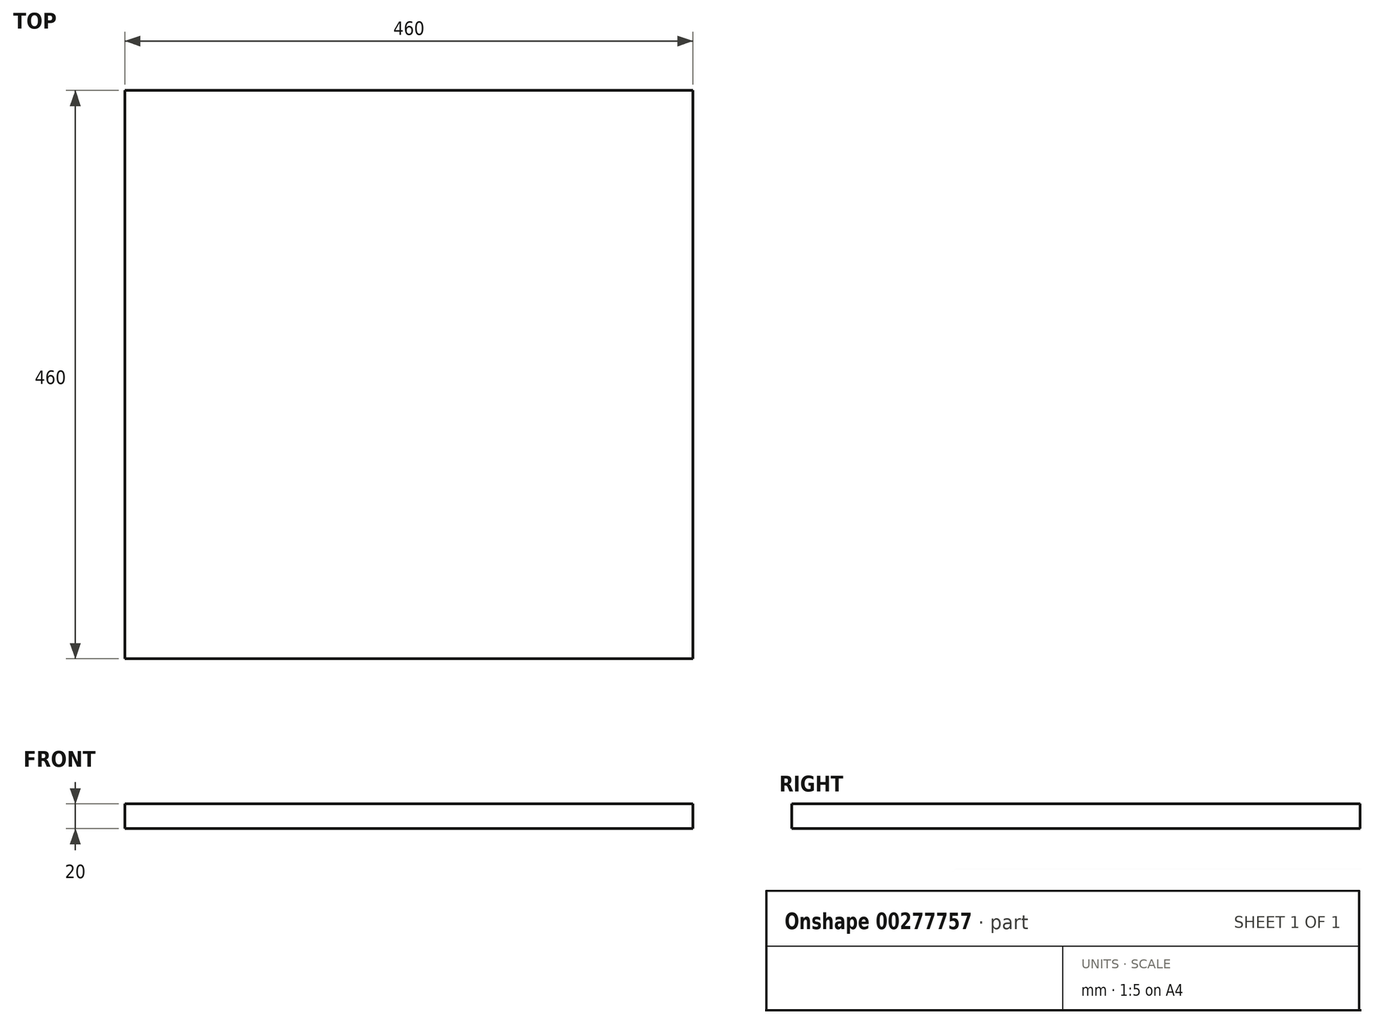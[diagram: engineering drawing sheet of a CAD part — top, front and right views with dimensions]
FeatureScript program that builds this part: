
annotation { "Feature Type Name" : "Feature", "Feature Type Description" : "" }
export const myFeature = defineFeature(function(context is Context, id is Id, definition is map)
    precondition{}
    {
        {
            var Q0;
            Q0=qCreatedBy(makeId("Top.planeOp"),FACE);
            var sketch = newSketch(context, id + "F0", { "sketchPlane" : qUnion([Q0])});
            skLineSegment(sketch, "E0.bottom", {"start": v(230, 230) * mm, "end": v(-230, 230) * mm});
            skLineSegment(sketch, "E0.top", {"start": v(230, -230) * mm, "end": v(-230, -230) * mm});
            skLineSegment(sketch, "E0.left", {"start": v(230, 230) * mm, "end": v(230, -230) * mm});
            skLineSegment(sketch, "E0.right", {"start": v(-230, 230) * mm, "end": v(-230, -230) * mm});
            skPoint(sketch, "E0.middle", {"position": v(0, 0) * mm});
            skSolve(sketch);
        }
        {
            var Q0;
            Q0 = qSketchRegion(id + "F0", true);
            extrude(context, id + "F1", {"entities" : qUnion([Q0]), "depth" : 20 * mm});
        }
    });
